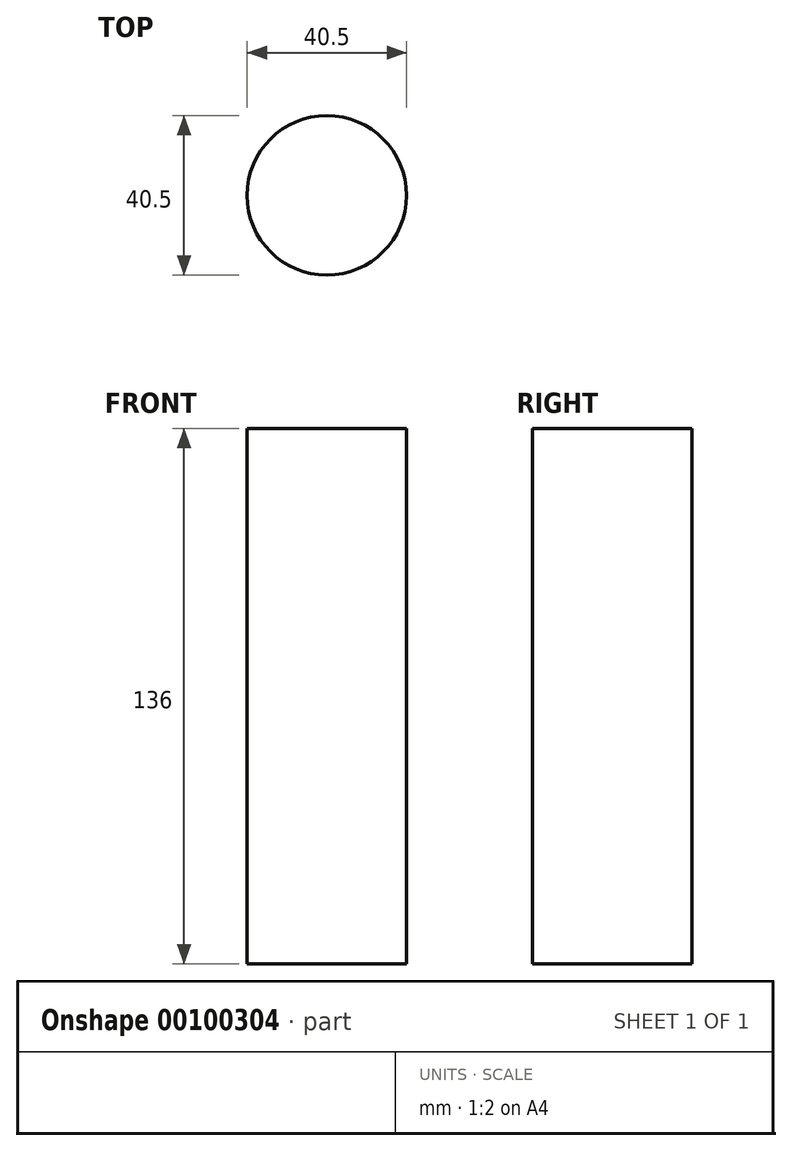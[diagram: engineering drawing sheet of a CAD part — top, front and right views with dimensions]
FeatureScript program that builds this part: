
annotation { "Feature Type Name" : "Feature", "Feature Type Description" : "" }
export const myFeature = defineFeature(function(context is Context, id is Id, definition is map)
    precondition{}
    {
        {
            var Q0;
            Q0=qCreatedBy(makeId("Front.planeOp"),FACE);
            var sketch = newSketch(context, id + "F0", { "sketchPlane" : qUnion([Q0])});
            skLineSegment(sketch, "E0", {"start": v(0, 76) * mm, "end": v(-20.25, 76) * mm});
            skLineSegment(sketch, "E1", {"start": v(-20.25, 76) * mm, "end": v(-20.25, -60) * mm});
            skLineSegment(sketch, "E2", {"start": v(-20.25, -60) * mm, "end": v(0, -60) * mm});
            skLineSegment(sketch, "E3", {"start": v(0, -60) * mm, "end": v(0, 76) * mm});
            skSolve(sketch);
        }
        {
            var Q0;
            Q0=makeQuery(id+"F0.imprint","IMPRINT",FACE,{"disambiguationData":[TD([[makeQuery(id+"F0.imprint","IMPRINT",EDGE,{"derivedFrom":sQuery(id+"F0.wireOp",EDGE,"E0")}),1.0]])]});
            var Q1;
            Q1=sQuery(id+"F0.wireOp",EDGE,"E3");
            revolve(context, id + "F1", {"entities" : qUnion([Q0]), "axis" : qUnion([Q1]), "revolveType" : RevolveType.FULL});
        }
    });
